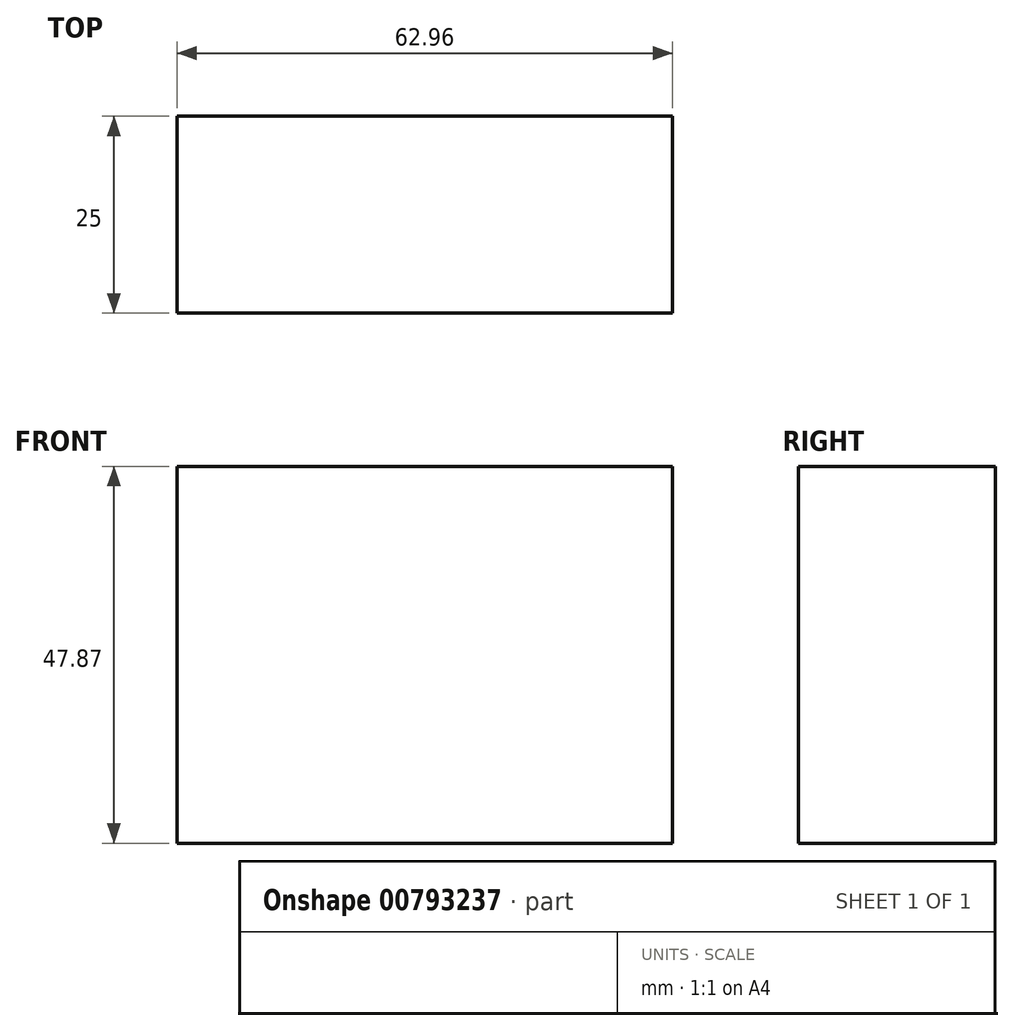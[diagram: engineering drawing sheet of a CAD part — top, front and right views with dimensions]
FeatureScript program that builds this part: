
annotation { "Feature Type Name" : "Feature", "Feature Type Description" : "" }
export const myFeature = defineFeature(function(context is Context, id is Id, definition is map)
    precondition{}
    {
        {
            var Q0;
            Q0=qCreatedBy(makeId("Front.planeOp"),FACE);
            var sketch = newSketch(context, id + "F0", { "sketchPlane" : qUnion([Q0])});
            skLineSegment(sketch, "E0.bottom", {"start": v(0, 0) * mm, "end": v(62.96, 0) * mm});
            skLineSegment(sketch, "E0.top", {"start": v(0, -47.87) * mm, "end": v(62.96, -47.87) * mm});
            skLineSegment(sketch, "E0.left", {"start": v(0, 0) * mm, "end": v(0, -47.87) * mm});
            skLineSegment(sketch, "E0.right", {"start": v(62.96, 0) * mm, "end": v(62.96, -47.87) * mm});
            skSolve(sketch);
        }
        {
            var Q0;
            Q0 = qSketchRegion(id + "F0", true);
            extrude(context, id + "F1", {"entities" : qUnion([Q0]), "depth" : 25 * mm, "offsetDistance" : 25 * mm});
        }
    });
